# Revit family: Faucet-Lavatory-American_Standard-Monterrey-750017X_Series
name_source: partatom
category: Plumbing Fixtures
units: mm (PartAtom-declared; Revit-internal decimal feet)

## family parameters
Always vertical = No
Cut with Voids When Loaded = No
OmniClass Number = 23.45.55.17
OmniClass Title = Mixing Faucets
Part Type = Normal
Room Calculation Point = No
Round Connector Dimension = Use Diameter
Shared = Yes
Work Plane-Based = No

## types (2) — shared parameters
ADA Compliant = Yes
Assembly Code = D2020300
CW Connection = Yes
CWFU = 1.5
CalGreen Compliant = No
Cold Water Connection Diameter = 1/2"
Compliance Certifications = ASME A112.18.1, CSA B 125, NSF 372, ANSI A117.1
Finish = Brass-American Standard-002-Polished Chrome
HW Connection = Yes
HWFU = 1.5
Handle Length = 4"
Height = 10 3/4"
Hot Water Connection Diameter = 1/2"
Installation Type = Deck Mounted
Manufacturer = American Standard
Material = Brass-American Standard-002-Polished Chrome
Price = Prices may vary. Please consult Manufacturer Representative for most up-to-date price list.
Product Documentation Link = https://lixil.cdn.celum.cloud
Product Page URL = https://www.americanstandard-us.com
Reach Height = 6 3/4"
Revised Date = 05/21/2024
Spout Reach = 5"
URL = https://www.americanstandard-us.com
Vandal-Resistant Wrist Blade handles = Yes
Vent Connection = No
Waste Connection = No
Width = 11 3/4"
zero-valued in all types: WFU

## per-type parameters (varying)
| type | Description | Flow Rate |
| 7500170.002 | Monterrey® 4-Inch Centerset Gooseneck Faucet With Wrist Blade Handles 1.5 gpm/5.7 Lpm | 1.5 gpm (5.7L/min) |
| 7500174.002 | Monterrey® 4-Inch Centerset Gooseneck Faucet With Wrist Blade Handles 0.35 gpm/1.3 Lpm | 0.35 gpm/1.3L/min |

note: column(s) folded — value = type name in every type: Model

## geometry (parser evidence)
native form markers: Sweep x2
no freeform markers — native parametric forms only
